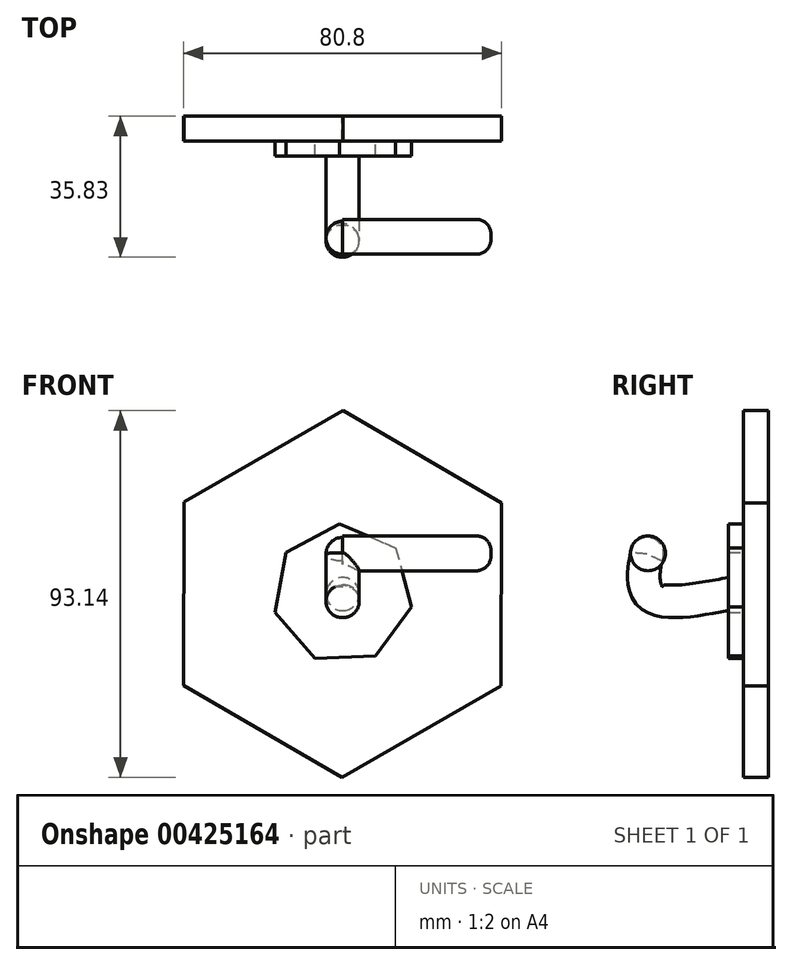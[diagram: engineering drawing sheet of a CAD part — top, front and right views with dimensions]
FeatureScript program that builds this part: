
annotation { "Feature Type Name" : "Feature", "Feature Type Description" : "" }
export const myFeature = defineFeature(function(context is Context, id is Id, definition is map)
    precondition{}
    {
        {
            var Q0;
            Q0=qCreatedBy(makeId("Front.planeOp"),FACE);
            var sketch = newSketch(context, id + "F0", { "sketchPlane" : qUnion([Q0])});
            skCircle(sketch, "E0.cCircle", {"center": v(0, 0) * mm, "radius": 40.33 * mm, "construction": true});
            skLineSegment(sketch, "E0.0", {"start": v(-40.26, 23.4) * mm, "end": v(0.14, 46.57) * mm});
            skLineSegment(sketch, "E0.1", {"start": v(0.14, 46.57) * mm, "end": v(40.4, 23.17) * mm});
            skLineSegment(sketch, "E0.2", {"start": v(40.4, 23.17) * mm, "end": v(40.26, -23.4) * mm});
            skLineSegment(sketch, "E0.3", {"start": v(40.26, -23.4) * mm, "end": v(-0.14, -46.57) * mm});
            skLineSegment(sketch, "E0.4", {"start": v(-0.14, -46.57) * mm, "end": v(-40.4, -23.17) * mm});
            skLineSegment(sketch, "E0.5", {"start": v(-40.4, -23.17) * mm, "end": v(-40.26, 23.4) * mm});
            skPoint(sketch, "E0.0.midPoint", {"position": v(-20.06, 34.99) * mm});
            skSolve(sketch);
        }
        {
            var Q0;
            Q0=makeQuery(id+"F0.imprint","IMPRINT",FACE,{"disambiguationData":[TD([[makeQuery(id+"F0.imprint","IMPRINT",EDGE,{"derivedFrom":sQuery(id+"F0.wireOp",EDGE,"E0.0")}),-1.0]])]});
            extrude(context, id + "F1", {"entities" : qUnion([Q0]), "depth" : 6.35 * mm});
        }
        {
            var Q0;
            Q0=makeQuery(id+"F1.opExtrude","CAP_FACE",FACE,{"disambiguationData":[OSD([sQuery(id+"F0.wireOp",EDGE,"E0.0"),sQuery(id+"F0.wireOp",EDGE,"E0.1"),sQuery(id+"F0.wireOp",EDGE,"E0.2"),sQuery(id+"F0.wireOp",EDGE,"E0.3"),sQuery(id+"F0.wireOp",EDGE,"E0.4"),sQuery(id+"F0.wireOp",EDGE,"E0.5")])],"isStart":false});
            var sketch = newSketch(context, id + "F2", { "sketchPlane" : qUnion([Q0])});
            skCircle(sketch, "E1.cCircle", {"center": v(0, 0) * mm, "radius": 16.1 * mm, "construction": true});
            skLineSegment(sketch, "E1.0", {"start": v(-14.42, 10.54) * mm, "end": v(-0.75, 17.84) * mm});
            skLineSegment(sketch, "E1.1", {"start": v(-0.75, 17.84) * mm, "end": v(13.48, 11.71) * mm});
            skLineSegment(sketch, "E1.2", {"start": v(13.48, 11.71) * mm, "end": v(17.56, -3.24) * mm});
            skLineSegment(sketch, "E1.3", {"start": v(17.56, -3.24) * mm, "end": v(8.42, -15.75) * mm});
            skLineSegment(sketch, "E1.4", {"start": v(8.42, -15.75) * mm, "end": v(-7.07, -16.4) * mm});
            skLineSegment(sketch, "E1.5", {"start": v(-7.07, -16.4) * mm, "end": v(-17.23, -4.7) * mm});
            skLineSegment(sketch, "E1.6", {"start": v(-17.23, -4.7) * mm, "end": v(-14.42, 10.54) * mm});
            skPoint(sketch, "E1.0.midPoint", {"position": v(-7.59, 14.2) * mm});
            skSolve(sketch);
        }
        {
            var Q0;
            Q0 = qSketchRegion(id + "F2", true);
            extrude(context, id + "F3", {"entities" : qUnion([Q0]), "operationType" : NewBodyOperationType.ADD, "depth" : 3.8 * mm});
        }
        {
            var Q0;
            Q0=makeQuery(id+"F3.opExtrude","CAP_FACE",FACE,{"disambiguationData":[OSD([sQuery(id+"F2.wireOp",EDGE,"E1.0"),sQuery(id+"F2.wireOp",EDGE,"E1.1"),sQuery(id+"F2.wireOp",EDGE,"E1.2"),sQuery(id+"F2.wireOp",EDGE,"E1.3"),sQuery(id+"F2.wireOp",EDGE,"E1.4"),sQuery(id+"F2.wireOp",EDGE,"E1.5"),sQuery(id+"F2.wireOp",EDGE,"E1.6")])],"isStart":false});
            var sketch = newSketch(context, id + "F4", { "sketchPlane" : qUnion([Q0])});
            skCircle(sketch, "E2", {"center": v(0, 0) * mm, "radius": 4.2 * mm});
            skSolve(sketch);
        }
        {
            var Q0;
            Q0=qCreatedBy(makeId("Right.planeOp"),FACE);
            var sketch = newSketch(context, id + "F5", { "sketchPlane" : qUnion([Q0])});
            skFitSpline(sketch, "E3", {"points": [v(-10.28, 0) * mm, v(-30.34, 0) * mm, v(-31.32, 8.07) * mm, v(-30.83, 10.28) * mm], "startDerivative": vector(-50.85, -9.45) * mm, "endDerivative": vector(2.66, 9.83) * mm});
            skSolve(sketch);
        }
        {
            var Q0;
            Q0=makeQuery(id+"F4.imprint","IMPRINT",FACE,{"disambiguationData":[TD([[makeQuery(id+"F4.imprint","IMPRINT",EDGE,{"derivedFrom":sQuery(id+"F4.wireOp",EDGE,"E2")}),1.0]])]});
            var Q1;
            Q1=sQuery(id+"F5.wireOp",EDGE,"E3");
            sweep(context, id + "F6", {"operationType" : NewBodyOperationType.ADD, "profiles" : qUnion([Q0]), "path" : qUnion([Q1])});
        }
        {
            var Q0;
            Q0=qCreatedBy(makeId("Right.planeOp"),FACE);
            var sketch = newSketch(context, id + "F7", { "sketchPlane" : qUnion([Q0])});
            skCircle(sketch, "E4", {"center": v(-30.65, 10.34) * mm, "radius": 4.42 * mm});
            skSolve(sketch);
        }
        {
            var Q0;
            Q0=makeQuery(id+"F6.opSweep","CAP_FACE",FACE,{"disambiguationData":[OSD([sQuery(id+"F4.wireOp",EDGE,"E2"),sQuery(id+"F5.wireOp",VERTEX,"E3.end")])],"isStart":false});
            var sketch = newSketch(context, id + "F8", { "sketchPlane" : qUnion([Q0])});
            skLineSegment(sketch, "E5", {"start": v(0, -32.24) * mm, "end": v(37.68, -32.24) * mm});
            skSolve(sketch);
        }
        {
            var Q0;
            Q0=makeQuery(id+"F7.imprint","IMPRINT",FACE,{"disambiguationData":[TD([[makeQuery(id+"F7.imprint","IMPRINT",EDGE,{"derivedFrom":sQuery(id+"F7.wireOp",EDGE,"E4")}),1.0]])]});
            var Q1;
            Q1=sQuery(id+"F8.wireOp",EDGE,"E5");
            sweep(context, id + "F9", {"operationType" : NewBodyOperationType.ADD, "profiles" : qUnion([Q0]), "path" : qUnion([Q1])});
        }
        {
            var Q0;
            Q0=makeQuery(id+"F6.opSweep","CAP_FACE",FACE,{"disambiguationData":[OSD([sQuery(id+"F4.wireOp",EDGE,"E2"),sQuery(id+"F5.wireOp",VERTEX,"E3.end")])],"isStart":false});
            var sketch = newSketch(context, id + "F10", { "sketchPlane" : qUnion([Q0])});
            skLineSegment(sketch, "E6", {"start": v(0, -14.18) * mm, "end": v(0, -59.2) * mm, "construction": true});
            skSolve(sketch);
        }
        {
            var Q0;
            {var subQ0=sQuery(id+"F5.wireOp",VERTEX,"E3.end");var subQ1=sQuery(id+"F4.wireOp",EDGE,"E2");Q0=makeQuery(id+"F10.imprint","IMPRINT",FACE,{"disambiguationData":[TD([[makeQuery(id+"F10.imprint","IMPRINT",EDGE,{"derivedFrom":makeQuery(id+"F6.opSweep","CAP_EDGE",EDGE,{"disambiguationData":[OSD([subQ1,subQ0])],"isStart":false})}),1.0]])]});}
            var Q1;
            Q1=sQuery(id+"F10.wireOp",EDGE,"E6");
            revolve(context, id + "F11", {"operationType" : NewBodyOperationType.ADD, "entities" : qUnion([Q0]), "axis" : qUnion([Q1]), "revolveType" : RevolveType.FULL});
        }
        {
            var Q0;
            Q0=makeQuery(id+"F9.opSweep","CAP_EDGE",EDGE,{"disambiguationData":[OSD([sQuery(id+"F7.wireOp",EDGE,"E4"),sQuery(id+"F8.wireOp",VERTEX,"E5.end")])],"isStart":false});
            fillet(context, id + "F12", {"entities" : qUnion([Q0]), "radius" : 3.68 * mm, "allowEdgeOverflow" : false});
        }
    });
